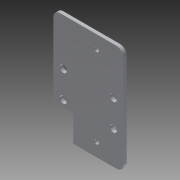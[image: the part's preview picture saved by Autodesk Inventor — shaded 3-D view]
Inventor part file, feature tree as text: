
AUTODESK INVENTOR PART (.ipt)
format: ipt  version: 2014 (Build 180170000, 170)  size: 128,512 bytes
history: native  units: in
note: dims shown in document units (in); Inventor stores cm internally (conversion verified against a paired STEP export)
features: extrude x3, sketch x2, fillet x1
ambient origin geometry x8: Origin, YZ Plane, XZ Plane, XY Plane, X Axis, Y Axis, Z Axis, Center Point
bodies: Solid1 (feature_tree)
feature tree (6):
  extrude  "Extrusion1"  Depth=2.63in
  extrude  "Extrusion4"  Depth=1.88in
  fillet  "Fillet1"  Radius=0.375in
  extrude  "Extrusion5"  Depth=1.0in
  sketch  "Sketch4"  dims[d0=1.5in d1=2.63in]
  sketch  "Sketch5"  dims[d2=1.0in d3=1.88in d4=0.375in d6=0.266in d7=0.266in d8=0.266in d9=0.266in d11=0.125in d12=0.0in d14=0.25in d15=0.375in d17=1.0in d18=4.0in d31=0.163in d32=1.0in d33=0.5in d34=0.163in d35=3.0in d36=1.0in d37=1.0in d38=0.0in d39=0.25in d40=1.0in d41=0.75in d42=1.0in d43=0.0in]
